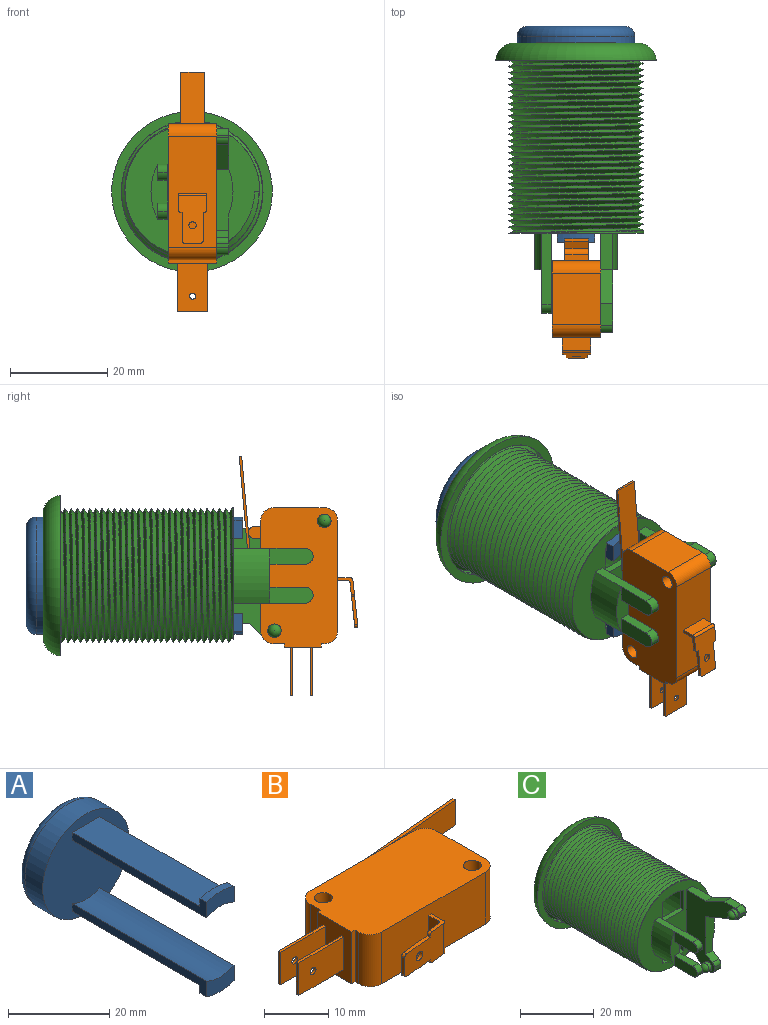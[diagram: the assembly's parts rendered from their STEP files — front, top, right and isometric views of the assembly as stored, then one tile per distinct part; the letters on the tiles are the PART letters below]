
ASSEMBLY  parts=3 mates=2
PART A: 64 faces, bbox 26.2x45.6x26.2 mm
  f0: sphere r=37.39mm, area 208.3mm2, adj f3,f18,f19,f20,f21,f22,f23,f24
  f1: plane 24.13x24.13mm, normal (0,-1,0), area 437.9mm2, adj f2,f5,f6,f7,f10,f11,f12,f14
  f2: cylinder r=12.06mm len=24.13mm, axis (0,-1,0), area 373.5mm2, adj f1,f3
  f3: torus R=10.06mm, axis (0,1,0), area 255.7mm2, adj f0,f2
  f4: cylinder r=12.06mm len=7.7mm, axis (0,1,0), area 14mm2, adj f5,f7,f8,f17
  f5: plane 37.5x3.78mm, normal (1,0,0), area 73.4mm2, adj f1,f4,f6,f8,f16,f17
  f6: cylinder r=8.56mm len=37.5mm, axis (0,1,0), area 299.5mm2, adj f1,f5,f7,f8
  f7: plane 37.5x3.78mm, normal (-1,0,0), area 73.4mm2, adj f1,f4,f6,f8,f16,f17
  f8: plane 7.7x4.42mm, normal (0,-1,0), area 27.6mm2, adj f4,f5,f6,f7
  f9: cylinder r=12.06mm len=7.7mm, axis (0,1,0), area 14mm2, adj f10,f12,f13,f15
  f10: plane 37.5x3.78mm, normal (-1,0,0), area 74.4mm2, adj f1,f9,f11,f13,f14,f15
  f11: cylinder r=8.56mm len=37.5mm, axis (0,1,0), area 299.5mm2, adj f1,f10,f12,f13
  f12: plane 37.5x3.78mm, normal (1,0,0), area 74.4mm2, adj f1,f9,f11,f13,f14,f15
  f13: plane 7.7x4.42mm, normal (0,-1,0), area 27.6mm2, adj f9,f10,f11,f12
  f14: plane 35.66x7.7mm, normal (0,0,1), area 274.6mm2, adj f1,f10,f12,f15
  f15: plane 7.73x2.56mm, normal (0,1,0.03), area 17.8mm2, adj f9,f10,f12,f14
  f16: plane 35.66x7.7mm, normal (0,0,-1), area 274.6mm2, adj f1,f5,f7,f17
  f17: plane 7.73x2.58mm, normal (0,1,-0.03), area 18mm2, adj f4,f5,f7,f16
  f18: extruded ~1.2x0.74mm, area 1.3mm2, adj f0,f19,f35,f37
  f19: plane 4.15x1.35mm, normal (-1,0,0), area 5.4mm2, adj f0,f18,f20,f35
  f20: extruded ~1.34x0.74mm, area 1.5mm2, adj f0,f19,f21,f35
  f21: plane 1.28x0.16mm, normal (0,0,-1), area 0.2mm2, adj f0,f20,f22,f35
  f22: plane 4.08x1.3mm, normal (1,0,0), area 5.2mm2, adj f0,f21,f23,f35
  f23: plane 1.21x0.4mm, normal (0,0,-1), area 0.5mm2, adj f0,f22,f24,f35
  f24: plane 9.23x1.27mm, normal (-1,0,0), area 10.3mm2, adj f0,f23,f25,f35
  f25: plane 1.09x0.66mm, normal (0,0,-1), area 0.7mm2, adj f0,f24,f26,f35
  f26: plane 5.69x1.18mm, normal (1,0,0), area 5.3mm2, adj f0,f25,f27,f35
  f27: plane 1.15x0.42mm, normal (0,0,-1), area 0.5mm2, adj f0,f26,f28,f35
  f28: plane 5.69x1.13mm, normal (-1,0,0), area 5mm2, adj f0,f27,f29,f35
  f29: plane 1.09x0.51mm, normal (0,0,-1), area 0.5mm2, adj f0,f28,f30,f35
  f30: plane 9.23x0.97mm, normal (1,0,0), area 7.5mm2, adj f0,f29,f31,f35
  f31: plane 0.89x0.41mm, normal (0,0,-1), area 0.3mm2, adj f0,f30,f32,f35
  f32: plane 4.08x0.91mm, normal (-1,0,0), area 3.6mm2, adj f0,f31,f33,f35
  f33: plane 0.88x0.16mm, normal (0,0,-1), area 0.1mm2, adj f0,f32,f34,f35
  f34: extruded ~0.85x0.73mm, area 0.9mm2, adj f0,f33,f35,f36
  f35: plane 10.74x5.21mm, normal (0,1,0), area 36.5mm2, adj f18,f19,f20,f21,f22,f23,f24,f25
  f36: plane 4.15x0.75mm, normal (1,0,0), area 3mm2, adj f0,f34,f35,f38
  f37: plane 3.75x1.09mm, normal (0,0,1), area 3.4mm2, adj f0,f18,f35,f38
  f38: extruded ~0.73x0.72mm, area 0.7mm2, adj f0,f35,f36,f37
  f39: plane 2.46x2.46mm, normal (0,1,0), area 4.8mm2, adj f40
  f40: extruded ~2.46x2.46mm, area 5.5mm2, adj f0,f39
  f41: plane 2.46x2.46mm, normal (0,1,0), area 4.8mm2, adj f42
  f42: extruded ~2.46x2.46mm, area 5.5mm2, adj f0,f41
  f43: plane 4.15x0.75mm, normal (-1,0,0), area 3mm2, adj f0,f44,f60,f61
  f44: extruded ~0.85x0.73mm, area 0.9mm2, adj f0,f43,f45,f61
  f45: plane 0.88x0.16mm, normal (0,0,-1), area 0.1mm2, adj f0,f44,f46,f61
  f46: plane 4.08x0.91mm, normal (1,0,0), area 3.6mm2, adj f0,f45,f47,f61
  f47: plane 0.89x0.41mm, normal (0,0,-1), area 0.3mm2, adj f0,f46,f48,f61
  f48: plane 9.23x0.97mm, normal (-1,0,0), area 7.5mm2, adj f0,f47,f49,f61
  f49: plane 1.09x0.51mm, normal (0,0,-1), area 0.5mm2, adj f0,f48,f50,f61
  f50: plane 5.69x1.13mm, normal (1,0,0), area 5mm2, adj f0,f49,f51,f61
  f51: plane 1.15x0.42mm, normal (0,0,-1), area 0.5mm2, adj f0,f50,f52,f61
  f52: plane 5.69x1.18mm, normal (-1,0,0), area 5.3mm2, adj f0,f51,f53,f61
  f53: plane 1.09x0.66mm, normal (0,0,-1), area 0.7mm2, adj f0,f52,f54,f61
  f54: plane 9.23x1.27mm, normal (1,0,0), area 10.3mm2, adj f0,f53,f55,f61
  f55: plane 1.21x0.4mm, normal (0,0,-1), area 0.5mm2, adj f0,f54,f56,f61
  f56: plane 4.08x1.3mm, normal (-1,0,0), area 5.2mm2, adj f0,f55,f57,f61
  f57: plane 1.28x0.16mm, normal (0,0,-1), area 0.2mm2, adj f0,f56,f58,f61
  f58: extruded ~1.34x0.74mm, area 1.5mm2, adj f0,f57,f59,f61
  f59: plane 4.15x1.35mm, normal (1,0,0), area 5.4mm2, adj f0,f58,f61,f62
  f60: extruded ~0.73x0.72mm, area 0.7mm2, adj f0,f43,f61,f63
  f61: plane 10.74x5.21mm, normal (0,1,0), area 36.5mm2, adj f43,f44,f45,f46,f47,f48,f49,f50
  f62: extruded ~1.2x0.74mm, area 1.3mm2, adj f0,f59,f61,f63
  f63: plane 3.75x1.09mm, normal (0,0,1), area 3.4mm2, adj f0,f60,f61,f62
PART B: 60 faces, bbox 49.2x24.4x9.9 mm
  f0: cylinder r=0.51mm len=0.69mm, axis (-0.11,0.99,0), area 0.5mm2, adj f3,f4,f49,f56
  f1: cylinder r=0.51mm len=5.84mm, axis (0,0,-1), area 4.3mm2, adj f4,f49,f50,f52
  f2: cylinder r=0.51mm len=0.69mm, axis (0.11,-0.99,0), area 0.5mm2, adj f3,f4,f50,f53
  f3: plane 9.71x5.84mm, normal (0.11,-0.99,0), area 45.3mm2, adj f0,f2,f41,f42,f43,f48,f49,f50
  f4: plane 9.14x5.84mm, normal (-0.11,0.99,0), area 42mm2, adj f0,f1,f2,f41,f42,f48,f49,f50
  f5: plane 2.54x2.54mm, normal (0,0,1), area 5.7mm2, adj f7,f8,f9,f38
  f6: plane 2.54x2.54mm, normal (0,0,-1), area 5.7mm2, adj f7,f8,f9,f38
  f7: plane 4.83x1.27mm, normal (-1,0,0), area 6.1mm2, adj f5,f6,f8,f38
  f8: cylinder r=1.27mm len=4.83mm, axis (0,0,1), area 19.3mm2, adj f5,f6,f7,f9
  f9: plane 4.83x1.27mm, normal (1,0,0), area 6.1mm2, adj f5,f6,f8,f38
  f10: plane 27.59x4.45mm, normal (0,0,1), area 14.8mm2, adj f12,f13,f14,f15,f16,f38,f44,f45
  f11: plane 27.59x4.45mm, normal (0,0,-1), area 14.8mm2, adj f12,f13,f14,f15,f16,f38,f44,f45
  f12: plane 4.83x0.51mm, normal (1,0.09,0), area 2.5mm2, adj f10,f11,f13,f16
  f13: plane 26.62x4.83mm, normal (0.09,-1,0), area 129.1mm2, adj f10,f11,f12,f44
  f14: plane 4.83x1.06mm, normal (1,0,0), area 5.1mm2, adj f10,f11,f38,f44
  f15: plane 4.83x1.52mm, normal (-1,0,0), area 7.4mm2, adj f10,f11,f38,f45
  f16: plane 27.08x4.83mm, normal (-0.09,1,0), area 131.3mm2, adj f10,f11,f12,f45
  f17: plane 9.91x0.51mm, normal (0,0,1), area 5mm2, adj f19,f20,f21,f34
  f18: plane 9.91x0.51mm, normal (0,0,-1), area 5mm2, adj f19,f20,f21,f34
  f19: plane 9.91x6.21mm, normal (0,1,0), area 60.2mm2, adj f17,f18,f21,f34,f47
  f20: plane 9.91x6.21mm, normal (0,-1,0), area 60.2mm2, adj f17,f18,f21,f34,f47
  f21: plane 6.21x0.51mm, normal (-1,0,0), area 3.2mm2, adj f17,f18,f19,f20
  f22: plane 9.91x0.51mm, normal (0,0,1), area 5mm2, adj f24,f25,f26,f34
  f23: plane 9.91x0.51mm, normal (0,0,-1), area 5mm2, adj f24,f25,f26,f34
  f24: plane 9.91x6.21mm, normal (0,1,0), area 60.2mm2, adj f22,f23,f26,f34,f46
  f25: plane 9.91x6.21mm, normal (0,-1,0), area 60.2mm2, adj f22,f23,f26,f34,f46
  f26: plane 6.21x0.51mm, normal (-1,0,0), area 3.2mm2, adj f22,f23,f24,f25
  f27: plane 28.7x15.75mm, normal (0,0,1), area 428mm2, adj f29,f30,f31,f32,f33,f34,f35,f36
  f28: plane 28.7x15.75mm, normal (0,0,-1), area 428mm2, adj f29,f30,f31,f32,f33,f34,f35,f36
  f29: cylinder r=2.54mm len=9.91mm, axis (0,0,1), area 39.5mm2, adj f27,f28,f30,f40
  f30: plane 22.86x9.91mm, normal (0,-1,0), area 222.8mm2, adj f27,f28,f29,f31,f49,f50,f51,f52
  f31: cylinder r=2.54mm len=9.91mm, axis (0,0,1), area 39.5mm2, adj f27,f28,f30,f32
  f32: plane 9.91x0.76mm, normal (-1,0,0), area 7.6mm2, adj f27,f28,f31,f33
  f33: plane 9.91x0.76mm, normal (0,-1,0), area 7.6mm2, adj f27,f28,f32,f34
  f34: plane 9.91x7.62mm, normal (-1,0,0), area 69.2mm2, adj f17,f18,f19,f20,f22,f23,f24,f25
  f35: plane 9.91x0.76mm, normal (0,1,0), area 7.6mm2, adj f27,f28,f34,f36
  f36: plane 9.91x2.29mm, normal (-1,0,0), area 22.7mm2, adj f27,f28,f35,f37
  f37: cylinder r=2.54mm len=9.91mm, axis (0,0,1), area 39.5mm2, adj f27,f28,f36,f38
  f38: plane 22.86x9.91mm, normal (0,1,0), area 211.8mm2, adj f5,f6,f7,f9,f10,f11,f14,f15
  f39: cylinder r=2.54mm len=9.91mm, axis (0,0,1), area 39.5mm2, adj f27,f28,f38,f40
  f40: plane 10.67x9.91mm, normal (1,0,0), area 105.7mm2, adj f27,f28,f29,f39
  f41: cylinder r=0.51mm len=0.69mm, axis (0.11,-0.99,0), area 0.5mm2, adj f3,f4,f48,f55
  f42: cylinder r=0.51mm len=0.69mm, axis (0.11,-0.99,0), area 0.5mm2, adj f3,f4,f48,f54
  f43: cylinder r=0.51mm len=5.84mm, axis (0,0,1), area 4.3mm2, adj f3,f49,f50,f51
  f44: cylinder r=0.51mm len=4.83mm, axis (0,0,-1), area 3.6mm2, adj f10,f11,f13,f14
  f45: cylinder r=0.51mm len=4.83mm, axis (0,0,1), area 3.6mm2, adj f10,f11,f15,f16
  f46: cylinder r=0.64mm len=1.27mm, axis (0,1,0), area 2mm2, adj f24,f25
  f47: cylinder r=0.64mm len=1.27mm, axis (0,1,0), area 2mm2, adj f19,f20
  f48: plane 3.3x0.63mm, normal (-0.99,-0.11,0), area 2.1mm2, adj f3,f4,f41,f42
  f49: plane 3.47x3.41mm, normal (0,0,-1), area 3.7mm2, adj f0,f1,f3,f4,f30,f43,f51,f52
  f50: plane 3.47x3.41mm, normal (0,0,1), area 3.7mm2, adj f1,f2,f3,f4,f30,f43,f51,f52
  f51: plane 5.84x2.65mm, normal (1,0,0), area 15.5mm2, adj f30,f43,f49,f50
  f52: plane 5.84x2.08mm, normal (-1,0,0), area 12.2mm2, adj f1,f30,f49,f50
  f53: plane 0.63x0.25mm, normal (-0.99,-0.11,0), area 0.2mm2, adj f2,f3,f4,f54
  f54: plane 5.88x1.26mm, normal (0,0,1), area 3.7mm2, adj f3,f4,f42,f53
  f55: plane 5.88x1.26mm, normal (0,0,-1), area 3.7mm2, adj f3,f4,f41,f56
  f56: plane 0.63x0.25mm, normal (-0.99,-0.11,0), area 0.2mm2, adj f0,f3,f4,f55
  f57: cylinder r=0.76mm len=1.58mm, axis (-0.11,0.99,0), area 3mm2, adj f3,f4
  f58: cylinder r=1.4mm len=9.91mm, axis (0,0,-1), area 86.9mm2, adj f27,f28
  f59: cylinder r=1.4mm len=9.91mm, axis (0,0,-1), area 86.9mm2, adj f27,f28
PART C: 64 faces, bbox 36.6x60.3x36.6 mm
  f0: plane 20.4x8.44mm, normal (1,0,0), area 100.3mm2, adj f5,f6,f34,f36,f51,f52,f55,f58
  f1: plane 11.35x3.36mm, normal (0,-1,0), area 19.7mm2, adj f3,f31,f41,f42,f45,f46
  f2: plane 7.5x0mm, normal (1,0,0), area 0mm2, adj f32,f44
  f3: plane 16.4x8mm, normal (1,0,0), area 88.5mm2, adj f1,f5,f30,f42,f44,f49,f50
  f4: plane 26x20.4mm, normal (-1,0,0), area 217.2mm2, adj f5,f7,f34,f35,f36,f37,f39,f51
  f5: plane 28.6x27.92mm, normal (0,-1,0), area 378.4mm2, adj f0,f3,f4,f6,f14,f15,f16,f17
  f6: cylinder r=12.52mm len=9.12mm, axis (0,1,0), area 70mm2, adj f0,f5,f7,f33
  f7: plane 12.49x3.36mm, normal (0,-1,0), area 36.5mm2, adj f4,f6,f33,f53,f55
  f8: plane 33.15x33.15mm, normal (0,-1,0), area 186.5mm2, adj f10,f11,f12,f13
  f9: plane 25.42x25.42mm, normal (0,1,0), area 20.7mm2, adj f10,f20
  f10: torus R=12.71mm, axis (0,-1,0), area 542.7mm2, adj f8,f9
  f11: plane 1.86x1.77mm, normal (0.31,0,-0.95), area 1.7mm2, adj f8,f12,f13,f16,f17,f18
  f12: bspline ~29.14x29.14mm, area 73.6mm2, adj f8,f11,f13,f18
  f13: bspline ~29.33x29.33mm, area 26.7mm2, adj f8,f11,f12
  f14: plane 1.1x0.65mm, normal (0,0,-1), area 0.4mm2, adj f5,f15,f17,f19
  f15: bspline ~27.98x19.88mm, area 8.2mm2, adj f5,f14,f16,f19
  f16: bspline ~36.7x27.59mm, area 2815.8mm2, adj f5,f11,f15,f17
  f17: bspline ~36.96x27.59mm, area 3151.4mm2, adj f5,f11,f14,f16,f18
  f18: bspline ~31.31x31.31mm, area 77.3mm2, adj f11,f12,f17
  f19: cylinder r=13.97mm len=27.22mm, axis (0,1,0), area 11.2mm2, adj f5,f14,f15
  f20: cylinder r=12.45mm len=37.7mm, axis (0,1,0), area 2948.3mm2, adj f9,f21
  f21: plane 24.89x24.89mm, normal (0,1,0), area 372.9mm2, adj f20,f22,f23,f24,f25,f26,f27,f28
  f22: cylinder r=10.92mm len=8.15mm, axis (0,-1,0), area 11.8mm2, adj f5,f21,f23,f25
  f23: plane 6.45x1.41mm, normal (-1,0,0), area 9.1mm2, adj f5,f21,f22,f24
  f24: plane 8.15x1.41mm, normal (0,0,1), area 11.5mm2, adj f5,f21,f23,f25
  f25: plane 6.45x1.41mm, normal (1,0,0), area 9.1mm2, adj f5,f21,f22,f24
  f26: plane 6.45x1.41mm, normal (-1,0,0), area 9.1mm2, adj f5,f21,f27,f29
  f27: cylinder r=10.92mm len=8.15mm, axis (0,-1,0), area 11.8mm2, adj f5,f21,f26,f28
  f28: plane 6.45x1.41mm, normal (1,0,0), area 9.1mm2, adj f5,f21,f27,f29
  f29: plane 8.15x1.41mm, normal (0,0,-1), area 11.5mm2, adj f5,f21,f26,f28
  f30: plane 14.65x2mm, normal (0,0,1), area 29.3mm2, adj f3,f5,f31,f41,f49
  f31: cylinder r=12.52mm len=11.35mm, axis (0,1,0), area 88.3mm2, adj f1,f5,f30,f32
  f32: plane 7.5x2mm, normal (0,0,-1), area 15mm2, adj f2,f5,f31,f43
  f33: plane 10.75x8.44mm, normal (1,0,0), area 60.2mm2, adj f5,f6,f7,f35,f53,f54,f56,f57
  f34: plane 4.49x2.5mm, normal (0,0,1), area 11.2mm2, adj f0,f4,f52,f58
  f35: plane 2.86x2.5mm, normal (0,0,-1), area 7.2mm2, adj f4,f33,f57,f61
  f36: plane 2.5x0.43mm, normal (0,-1,0), area 1.1mm2, adj f0,f4,f58,f59
  f37: cylinder r=1.37mm len=2.73mm, axis (1,0,0), area 9.8mm2, adj f4,f63
  f38: plane 0.01x0.01mm, normal (-1,0,0), area 0mm2, adj f63
  f39: cylinder r=1.37mm len=2.73mm, axis (1,0,0), area 9.8mm2, adj f4,f62
  f40: plane 0.01x0.01mm, normal (-1,0,0), area 0mm2, adj f62
  f41: plane 8.9x3.35mm, normal (-1,0,0), area 28.5mm2, adj f1,f30,f42,f49,f50
  f42: plane 7.15x2mm, normal (0,0,-1), area 14.3mm2, adj f1,f3,f41,f50
  f43: plane 7.15x2mm, normal (0,0,-1), area 14.3mm2, adj f32,f44,f46,f48
  f44: plane 16.4x3.35mm, normal (1,0,0), area 53.6mm2, adj f2,f3,f5,f43,f45,f47,f48
  f45: plane 7.15x2mm, normal (0,0,1), area 14.3mm2, adj f1,f44,f46,f47
  f46: plane 8.9x3.35mm, normal (-1,0,0), area 28.5mm2, adj f1,f43,f45,f47,f48
  f47: cylinder r=1.75mm len=2mm, axis (-1,0,0), area 5.3mm2, adj f44,f45,f46,f48
  f48: cylinder r=1.75mm len=2mm, axis (1,0,0), area 5.3mm2, adj f43,f44,f46,f47
  f49: cylinder r=1.75mm len=2mm, axis (-1,0,0), area 5.3mm2, adj f3,f30,f41,f50
  f50: cylinder r=1.75mm len=2mm, axis (1,0,0), area 5.3mm2, adj f3,f41,f42,f49
  f51: plane 7.5x2.5mm, normal (0,0,1), area 18.8mm2, adj f0,f4,f5,f52
  f52: plane 6.91x3.25mm, normal (0,0.43,0.9), area 19.1mm2, adj f0,f4,f34,f51
  f53: plane 2.52x2.5mm, normal (0,-0.51,0.86), area 7.3mm2, adj f4,f7,f33,f60
  f54: plane 2.5x0.78mm, normal (0,-1,0), area 1.9mm2, adj f4,f33,f60,f61
  f55: plane 11.99x5.13mm, normal (0,-0.39,-0.92), area 32.6mm2, adj f0,f4,f7,f59
  f56: plane 3.33x2.5mm, normal (0,0,-1), area 8.3mm2, adj f4,f5,f33,f57
  f57: plane 3.25x3.06mm, normal (0,0.73,-0.69), area 11.2mm2, adj f4,f33,f35,f56
  f58: cylinder r=1.5mm len=2.5mm, axis (-1,0,0), area 5.9mm2, adj f0,f4,f34,f36
  f59: cylinder r=1.5mm len=2.5mm, axis (1,0,0), area 4.4mm2, adj f0,f4,f36,f55
  f60: cylinder r=1.5mm len=2.5mm, axis (1,0,0), area 3.9mm2, adj f4,f33,f53,f54
  f61: cylinder r=1.5mm len=2.5mm, axis (1,0,0), area 5.9mm2, adj f4,f33,f35,f54
  f62: torus R=0.01mm, axis (-1,0,0), area 11.7mm2, adj f39,f40
  f63: torus R=0.01mm, axis (-1,0,0), area 11.7mm2, adj f37,f38
PLACE A t=(-21.53,12.77,-1.59)mm
PLACE B rot(axis=(0,-1,0),90deg) t=(-21.41,-36.37,-1.6)mm
PLACE C t=(-21.53,12.71,-1.59)mm
MATE fastened B.f59 <-> C.f39  axis (1,0,0) through (-16.45,-41.53,9.7)mm
MATE fastened A.f2 <-> C.f10  axis (0,-1,0) through (-21.53,12.77,-1.59)mm
